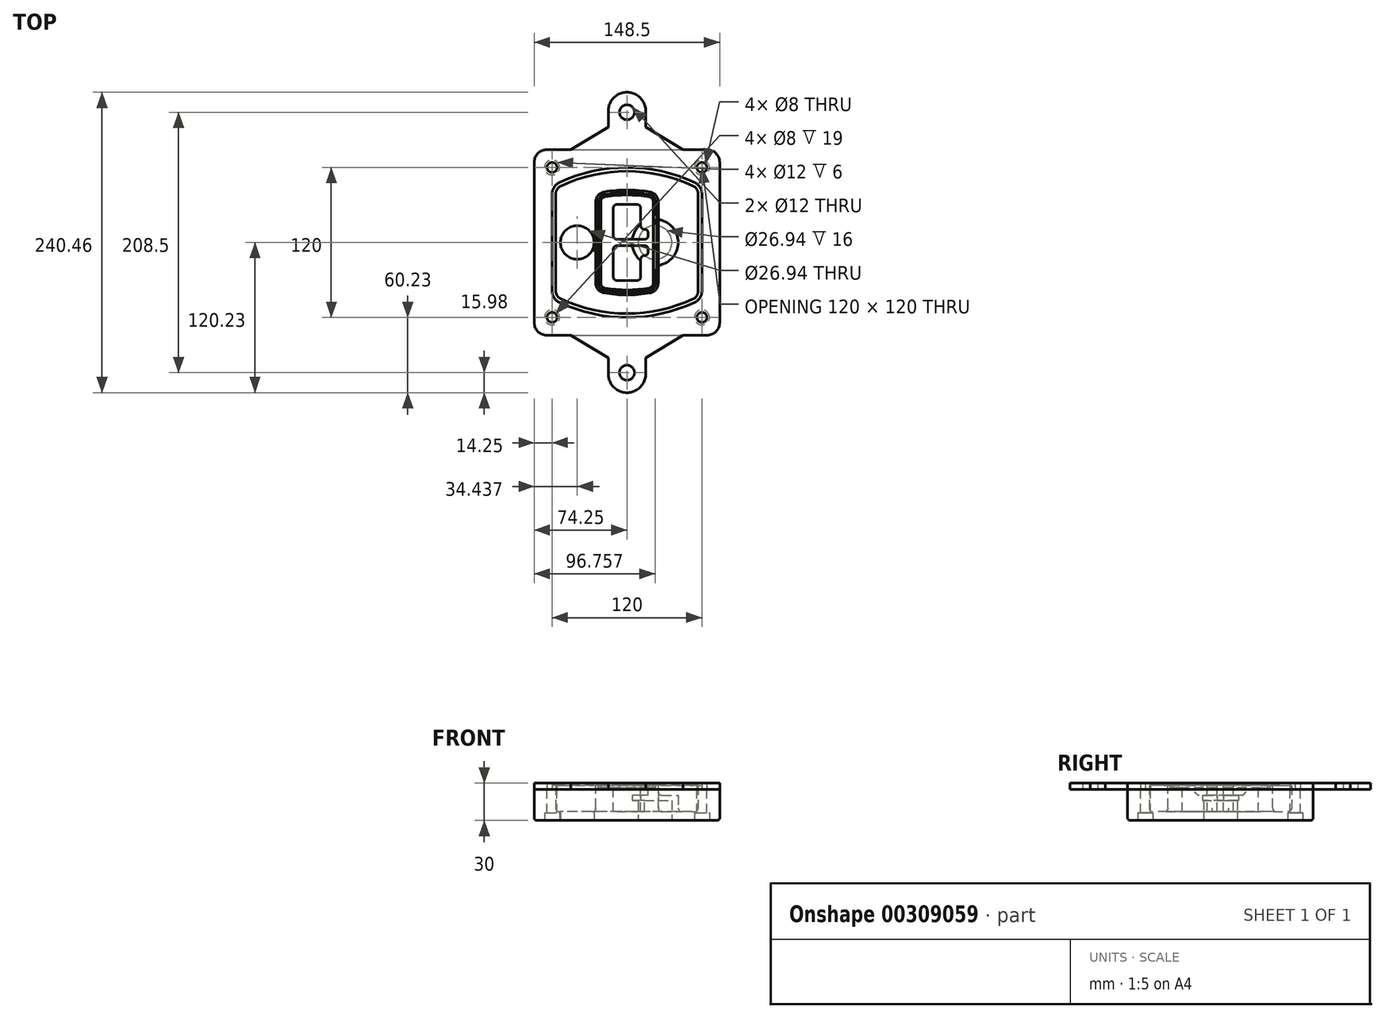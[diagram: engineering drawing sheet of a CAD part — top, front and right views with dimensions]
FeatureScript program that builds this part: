
annotation { "Feature Type Name" : "Feature", "Feature Type Description" : "" }
export const myFeature = defineFeature(function(context is Context, id is Id, definition is map)
    precondition{}
    {
        {
            var Q0;
            Q0=qCreatedBy(makeId("Top.planeOp"),FACE);
            var sketch = newSketch(context, id + "F0", { "sketchPlane" : qUnion([Q0])});
            skPoint(sketch, "E0.rect.middle", {"position": v(0, 0) * mm});
            skLineSegment(sketch, "E1.bottom", {"start": v(-64.25, -74.25) * mm, "end": v(64.25, -74.25) * mm});
            skLineSegment(sketch, "E1.top", {"start": v(-64.25, 74.25) * mm, "end": v(64.25, 74.25) * mm});
            skLineSegment(sketch, "E1.left", {"start": v(-74.25, -64.25) * mm, "end": v(-74.25, 64.25) * mm});
            skLineSegment(sketch, "E1.right", {"start": v(74.25, -64.25) * mm, "end": v(74.25, 64.25) * mm});
            skLineSegment(sketch, "E2", {"start": v(-74.25, 74.25) * mm, "end": v(74.25, -74.25) * mm, "construction": true});
            skLineSegment(sketch, "E3", {"start": v(74.25, 74.25) * mm, "end": v(-74.25, -74.25) * mm, "construction": true});
            skCircle(sketch, "E4", {"center": v(-60, 60) * mm, "radius": 4 * mm});
            skCircle(sketch, "E5", {"center": v(60, 60) * mm, "radius": 4 * mm});
            skCircle(sketch, "E6", {"center": v(60, -60) * mm, "radius": 4 * mm});
            skCircle(sketch, "E7", {"center": v(-60, -60) * mm, "radius": 4 * mm});
            skLineSegment(sketch, "E8", {"start": v(-60, 60) * mm, "end": v(60, 60) * mm, "construction": true});
            skLineSegment(sketch, "E9", {"start": v(60, 60) * mm, "end": v(60, -60) * mm, "construction": true});
            skLineSegment(sketch, "E10", {"start": v(60, -60) * mm, "end": v(-60, -60) * mm, "construction": true});
            skLineSegment(sketch, "E11", {"start": v(-60, -60) * mm, "end": v(-60, 60) * mm, "construction": true});
            skLineSegment(sketch, "E12", {"start": v(-60, 38.83) * mm, "end": v(-60, -38.83) * mm});
            skLineSegment(sketch, "E13", {"start": v(60, 38.83) * mm, "end": v(60, -38.83) * mm});
            skArc(sketch, "E14", {"start": v(54.26, 47.88) * mm, "mid": v(0, 60) * mm, "end": v(-54.26, 47.88) * mm});
            skArc(sketch, "E15", {"start": v(-54.26, -47.88) * mm, "mid": v(0, -60) * mm, "end": v(54.26, -47.88) * mm});
            skLineSegment(sketch, "E16", {"start": v(-60, 0) * mm, "end": v(60, 0) * mm, "construction": true});
            skPoint(sketch, "E17.visualSharp", {"position": v(-60, -45) * mm});
            skArc(sketch, "E17.filletArc", {"start": v(-60, -38.83) * mm, "mid": v(-58.44, -44.2) * mm, "end": v(-54.26, -47.88) * mm});
            skPoint(sketch, "E18.visualSharp", {"position": v(-60, 45) * mm});
            skArc(sketch, "E18.filletArc", {"start": v(-54.26, 47.88) * mm, "mid": v(-58.44, 44.2) * mm, "end": v(-60, 38.83) * mm});
            skPoint(sketch, "E19.visualSharp", {"position": v(60, 45) * mm});
            skArc(sketch, "E19.filletArc", {"start": v(60, 38.83) * mm, "mid": v(58.44, 44.2) * mm, "end": v(54.26, 47.88) * mm});
            skPoint(sketch, "E20.visualSharp", {"position": v(60, -45) * mm});
            skArc(sketch, "E20.filletArc", {"start": v(54.26, -47.88) * mm, "mid": v(58.44, -44.2) * mm, "end": v(60, -38.83) * mm});
            skPoint(sketch, "E21.visualSharp", {"position": v(-74.25, 74.25) * mm});
            skArc(sketch, "E21.filletArc", {"start": v(-64.25, 74.25) * mm, "mid": v(-71.32, 71.32) * mm, "end": v(-74.25, 64.25) * mm});
            skPoint(sketch, "E22.visualSharp", {"position": v(74.25, 74.25) * mm});
            skArc(sketch, "E22.filletArc", {"start": v(74.25, 64.25) * mm, "mid": v(71.32, 71.32) * mm, "end": v(64.25, 74.25) * mm});
            skPoint(sketch, "E23.visualSharp", {"position": v(74.25, -74.25) * mm});
            skArc(sketch, "E23.filletArc", {"start": v(64.25, -74.25) * mm, "mid": v(71.32, -71.32) * mm, "end": v(74.25, -64.25) * mm});
            skPoint(sketch, "E24.visualSharp", {"position": v(-74.25, -74.25) * mm});
            skArc(sketch, "E24.filletArc", {"start": v(-74.25, -64.25) * mm, "mid": v(-71.32, -71.32) * mm, "end": v(-64.25, -74.25) * mm});
            skArc(sketch, "E25.0", {"start": v(57, 38.83) * mm, "mid": v(55.9, 42.58) * mm, "end": v(52.98, 45.17) * mm});
            skLineSegment(sketch, "E25.1", {"start": v(57, 38.83) * mm, "end": v(57, -38.83) * mm});
            skArc(sketch, "E25.2", {"start": v(52.98, -45.17) * mm, "mid": v(55.9, -42.58) * mm, "end": v(57, -38.83) * mm});
            skArc(sketch, "E25.3", {"start": v(-52.98, -45.17) * mm, "mid": v(0, -57) * mm, "end": v(52.98, -45.17) * mm});
            skArc(sketch, "E25.4", {"start": v(-57, -38.83) * mm, "mid": v(-55.9, -42.58) * mm, "end": v(-52.98, -45.17) * mm});
            skArc(sketch, "E25.5", {"start": v(52.98, 45.17) * mm, "mid": v(0, 57) * mm, "end": v(-52.98, 45.17) * mm});
            skLineSegment(sketch, "E25.6", {"start": v(-57, 38.83) * mm, "end": v(-57, -38.83) * mm});
            skArc(sketch, "E25.7", {"start": v(-52.98, 45.17) * mm, "mid": v(-55.9, 42.58) * mm, "end": v(-57, 38.83) * mm});
            skArc(sketch, "E26.0", {"start": v(-55.96, 51.5) * mm, "mid": v(-61.82, 46.33) * mm, "end": v(-64, 38.83) * mm});
            skArc(sketch, "E26.1", {"start": v(55.96, 51.5) * mm, "mid": v(0, 64) * mm, "end": v(-55.96, 51.5) * mm});
            skArc(sketch, "E26.2", {"start": v(64, 38.83) * mm, "mid": v(61.82, 46.33) * mm, "end": v(55.96, 51.5) * mm});
            skLineSegment(sketch, "E26.3", {"start": v(64, 38.83) * mm, "end": v(64, -38.83) * mm});
            skArc(sketch, "E26.4", {"start": v(55.96, -51.5) * mm, "mid": v(61.82, -46.33) * mm, "end": v(64, -38.83) * mm});
            skLineSegment(sketch, "E26.5", {"start": v(-64, 38.83) * mm, "end": v(-64, -38.83) * mm});
            skArc(sketch, "E26.6", {"start": v(-55.96, -51.5) * mm, "mid": v(0, -64) * mm, "end": v(55.96, -51.5) * mm});
            skArc(sketch, "E26.7", {"start": v(-64, -38.83) * mm, "mid": v(-61.82, -46.33) * mm, "end": v(-55.96, -51.5) * mm});
            skSolve(sketch);
        }
        {
            var Q0;
            Q0=makeQuery(id+"F0.imprint","IMPRINT",FACE,{"disambiguationData":[TD([[makeQuery(id+"F0.imprint","IMPRINT",EDGE,{"derivedFrom":sQuery(id+"F0.wireOp",EDGE,"E1.bottom")}),1.0]])]});
            var Q1;
            Q1=makeQuery(id+"F0.imprint","IMPRINT",FACE,{"disambiguationData":[TD([[makeQuery(id+"F0.imprint","IMPRINT",EDGE,{"derivedFrom":sQuery(id+"F0.wireOp",EDGE,"E12")}),1.0]])]});
            var Q2;
            Q2=makeQuery(id+"F0.imprint","IMPRINT",FACE,{"disambiguationData":[TD([[makeQuery(id+"F0.imprint","IMPRINT",EDGE,{"derivedFrom":sQuery(id+"F0.wireOp",EDGE,"E25.0")}),1.0]])]});
            var Q3;
            Q3=makeQuery(id+"F0.imprint","IMPRINT",FACE,{"disambiguationData":[TD([[makeQuery(id+"F0.imprint","IMPRINT",EDGE,{"derivedFrom":sQuery(id+"F0.wireOp",EDGE,"E12")}),-1.0]])]});
            extrude(context, id + "F1", {"entities" : qUnion([Q0, Q1, Q2, Q3]), "oppositeDirection" : true, "depth" : 25 * mm});
        }
        {
            var Q0;
            Q0=makeQuery(id+"F0.imprint","IMPRINT",FACE,{"disambiguationData":[TD([[makeQuery(id+"F0.imprint","IMPRINT",EDGE,{"derivedFrom":sQuery(id+"F0.wireOp",EDGE,"E12")}),1.0]])]});
            extrude(context, id + "F2", {"entities" : qUnion([Q0]), "operationType" : NewBodyOperationType.ADD, "depth" : 3 * mm});
        }
        {
            var Q0;
            Q0=makeQuery(id+"F0.imprint","IMPRINT",FACE,{"disambiguationData":[TD([[makeQuery(id+"F0.imprint","IMPRINT",EDGE,{"derivedFrom":sQuery(id+"F0.wireOp",EDGE,"E25.0")}),1.0]])]});
            extrude(context, id + "F3", {"entities" : qUnion([Q0]), "operationType" : NewBodyOperationType.REMOVE, "oppositeDirection" : true, "depth" : 18 * mm});
        }
        {
            var Q0;
            Q0=makeQuery(id+"F2.opExtrude","CAP_FACE",FACE,{"disambiguationData":[OSD([sQuery(id+"F0.wireOp",EDGE,"E12"),sQuery(id+"F0.wireOp",EDGE,"E13"),sQuery(id+"F0.wireOp",EDGE,"E14"),sQuery(id+"F0.wireOp",EDGE,"E15"),sQuery(id+"F0.wireOp",EDGE,"E17.filletArc"),sQuery(id+"F0.wireOp",EDGE,"E18.filletArc"),sQuery(id+"F0.wireOp",EDGE,"E19.filletArc"),sQuery(id+"F0.wireOp",EDGE,"E20.filletArc"),sQuery(id+"F0.wireOp",EDGE,"E25.0"),sQuery(id+"F0.wireOp",EDGE,"E25.1"),sQuery(id+"F0.wireOp",EDGE,"E25.2"),sQuery(id+"F0.wireOp",EDGE,"E25.3"),sQuery(id+"F0.wireOp",EDGE,"E25.4"),sQuery(id+"F0.wireOp",EDGE,"E25.5"),sQuery(id+"F0.wireOp",EDGE,"E25.6"),sQuery(id+"F0.wireOp",EDGE,"E25.7")])],"isStart":false});
            var sketch = newSketch(context, id + "F4", { "sketchPlane" : qUnion([Q0])});
            skArc(sketch, "E27.0", {"start": v(-18.34, -40.45) * mm, "mid": v(0, -42) * mm, "end": v(18.34, -40.45) * mm});
            skArc(sketch, "E28.0", {"start": v(18.34, 40.45) * mm, "mid": v(0, 42) * mm, "end": v(-18.34, 40.45) * mm});
            skLineSegment(sketch, "E29", {"start": v(-25, 32.57) * mm, "end": v(-25, -32.57) * mm});
            skLineSegment(sketch, "E30", {"start": v(25, 32.57) * mm, "end": v(25, -32.57) * mm});
            skLineSegment(sketch, "E31", {"start": v(-25, 39.1) * mm, "end": v(25, 39.1) * mm, "construction": true});
            skLineSegment(sketch, "E32", {"start": v(-25, -39.1) * mm, "end": v(25, -39.1) * mm, "construction": true});
            skPoint(sketch, "E33.visualSharp", {"position": v(-25, 39.1) * mm});
            skArc(sketch, "E33.filletArc", {"start": v(-18.34, 40.45) * mm, "mid": v(-23.11, 37.73) * mm, "end": v(-25, 32.57) * mm});
            skPoint(sketch, "E34.visualSharp", {"position": v(25, 39.1) * mm});
            skArc(sketch, "E34.filletArc", {"start": v(25, 32.57) * mm, "mid": v(23.11, 37.73) * mm, "end": v(18.34, 40.45) * mm});
            skPoint(sketch, "E35.visualSharp", {"position": v(25, -39.1) * mm});
            skArc(sketch, "E35.filletArc", {"start": v(18.34, -40.45) * mm, "mid": v(23.11, -37.73) * mm, "end": v(25, -32.57) * mm});
            skPoint(sketch, "E36.visualSharp", {"position": v(-25, -39.1) * mm});
            skArc(sketch, "E36.filletArc", {"start": v(-25, -32.57) * mm, "mid": v(-23.11, -37.73) * mm, "end": v(-18.34, -40.45) * mm});
            skArc(sketch, "E37.0", {"start": v(52.98, 45.17) * mm, "mid": v(0, 57) * mm, "end": v(-52.98, 45.17) * mm});
            skArc(sketch, "E37.1", {"start": v(-52.98, 45.17) * mm, "mid": v(-55.9, 42.58) * mm, "end": v(-57, 38.83) * mm});
            skLineSegment(sketch, "E37.2", {"start": v(-57, 38.83) * mm, "end": v(-57, -38.83) * mm});
            skArc(sketch, "E37.3", {"start": v(-57, -38.83) * mm, "mid": v(-55.9, -42.58) * mm, "end": v(-52.98, -45.17) * mm});
            skArc(sketch, "E37.4", {"start": v(-52.98, -45.17) * mm, "mid": v(0, -57) * mm, "end": v(52.98, -45.17) * mm});
            skArc(sketch, "E37.5", {"start": v(52.98, -45.17) * mm, "mid": v(55.9, -42.58) * mm, "end": v(57, -38.83) * mm});
            skLineSegment(sketch, "E37.6", {"start": v(57, 38.83) * mm, "end": v(57, -38.83) * mm});
            skArc(sketch, "E37.7", {"start": v(57, 38.83) * mm, "mid": v(55.9, 42.58) * mm, "end": v(52.98, 45.17) * mm});
            skLineSegment(sketch, "E38.0", {"start": v(23, 32.57) * mm, "end": v(23, -32.57) * mm});
            skArc(sketch, "E38.1", {"start": v(18, -38.48) * mm, "mid": v(21.58, -36.44) * mm, "end": v(23, -32.57) * mm});
            skArc(sketch, "E38.2", {"start": v(-18, -38.48) * mm, "mid": v(0, -40) * mm, "end": v(18, -38.48) * mm});
            skArc(sketch, "E38.3", {"start": v(-23, -32.57) * mm, "mid": v(-21.58, -36.44) * mm, "end": v(-18, -38.48) * mm});
            skLineSegment(sketch, "E38.4", {"start": v(-23, 32.57) * mm, "end": v(-23, -32.57) * mm});
            skArc(sketch, "E38.5", {"start": v(23, 32.57) * mm, "mid": v(21.58, 36.44) * mm, "end": v(18, 38.48) * mm});
            skArc(sketch, "E38.6", {"start": v(-18, 38.48) * mm, "mid": v(-21.58, 36.44) * mm, "end": v(-23, 32.57) * mm});
            skArc(sketch, "E38.7", {"start": v(18, 38.48) * mm, "mid": v(0, 40) * mm, "end": v(-18, 38.48) * mm});
            skArc(sketch, "E39.0", {"start": v(21, 32.57) * mm, "mid": v(20.06, 35.15) * mm, "end": v(17.67, 36.5) * mm});
            skLineSegment(sketch, "E39.1", {"start": v(21, 32.57) * mm, "end": v(21, -32.57) * mm});
            skArc(sketch, "E39.2", {"start": v(17.67, -36.5) * mm, "mid": v(20.06, -35.15) * mm, "end": v(21, -32.57) * mm});
            skArc(sketch, "E39.3", {"start": v(-17.67, -36.5) * mm, "mid": v(0, -38) * mm, "end": v(17.67, -36.5) * mm});
            skArc(sketch, "E39.4", {"start": v(-21, -32.57) * mm, "mid": v(-20.06, -35.15) * mm, "end": v(-17.67, -36.5) * mm});
            skArc(sketch, "E39.5", {"start": v(17.67, 36.5) * mm, "mid": v(0, 38) * mm, "end": v(-17.67, 36.5) * mm});
            skLineSegment(sketch, "E39.6", {"start": v(-21, 32.57) * mm, "end": v(-21, -32.57) * mm});
            skArc(sketch, "E39.7", {"start": v(-17.67, 36.5) * mm, "mid": v(-20.06, 35.15) * mm, "end": v(-21, 32.57) * mm});
            skLineSegment(sketch, "E40", {"start": v(-25, 0) * mm, "end": v(25, 0) * mm, "construction": true});
            skLineSegment(sketch, "E41", {"start": v(-11, 5.5) * mm, "end": v(-11, 27.5) * mm});
            skLineSegment(sketch, "E42", {"start": v(-8, 30.5) * mm, "end": v(8, 30.5) * mm});
            skLineSegment(sketch, "E43", {"start": v(11, 27.5) * mm, "end": v(11, 13.5) * mm});
            skLineSegment(sketch, "E44", {"start": v(14, 10.5) * mm, "end": v(14, 10.5) * mm});
            skLineSegment(sketch, "E45", {"start": v(17, 7.5) * mm, "end": v(17, 5.5) * mm});
            skLineSegment(sketch, "E46", {"start": v(14, 2.5) * mm, "end": v(-8, 2.5) * mm});
            skPoint(sketch, "E47.visualSharp", {"position": v(-11, 30.5) * mm});
            skArc(sketch, "E47.filletArc", {"start": v(-8, 30.5) * mm, "mid": v(-10.12, 29.62) * mm, "end": v(-11, 27.5) * mm});
            skPoint(sketch, "E48.visualSharp", {"position": v(11, 30.5) * mm});
            skArc(sketch, "E48.filletArc", {"start": v(11, 27.5) * mm, "mid": v(10.12, 29.62) * mm, "end": v(8, 30.5) * mm});
            skPoint(sketch, "E49.visualSharp", {"position": v(11, 10.5) * mm});
            skArc(sketch, "E49.filletArc", {"start": v(11, 13.5) * mm, "mid": v(11.88, 11.38) * mm, "end": v(14, 10.5) * mm});
            skPoint(sketch, "E50.visualSharp", {"position": v(17, 10.5) * mm});
            skArc(sketch, "E50.filletArc", {"start": v(17, 7.5) * mm, "mid": v(16.12, 9.62) * mm, "end": v(14, 10.5) * mm});
            skPoint(sketch, "E51.visualSharp", {"position": v(17, 2.5) * mm});
            skArc(sketch, "E51.filletArc", {"start": v(14, 2.5) * mm, "mid": v(16.12, 3.38) * mm, "end": v(17, 5.5) * mm});
            skPoint(sketch, "E52.visualSharp", {"position": v(-11, 2.5) * mm});
            skArc(sketch, "E52.filletArc", {"start": v(-11, 5.5) * mm, "mid": v(-10.12, 3.38) * mm, "end": v(-8, 2.5) * mm});
            skLineSegment(sketch, "E53.0.MirrorCS", {"start": v(14, -2.5) * mm, "end": v(-8, -2.5) * mm});
            skArc(sketch, "E54.0.MirrorCS", {"start": v(-11, -5.5) * mm, "mid": v(-10.12, -3.38) * mm, "end": v(-8, -2.5) * mm});
            skLineSegment(sketch, "E55.0.MirrorCS", {"start": v(-11, -5.5) * mm, "end": v(-11, -27.5) * mm});
            skArc(sketch, "E56.0.MirrorCS", {"start": v(-8, -30.5) * mm, "mid": v(-10.12, -29.62) * mm, "end": v(-11, -27.5) * mm});
            skLineSegment(sketch, "E57.0.MirrorCS", {"start": v(-8, -30.5) * mm, "end": v(8, -30.5) * mm});
            skArc(sketch, "E58.0.MirrorCS", {"start": v(11, -27.5) * mm, "mid": v(10.12, -29.62) * mm, "end": v(8, -30.5) * mm});
            skLineSegment(sketch, "E59.0.MirrorCS", {"start": v(11, -27.5) * mm, "end": v(11, -13.5) * mm});
            skArc(sketch, "E60.0.MirrorCS", {"start": v(11, -13.5) * mm, "mid": v(11.88, -11.38) * mm, "end": v(14, -10.5) * mm});
            skArc(sketch, "E61.0.MirrorCS", {"start": v(17, -7.5) * mm, "mid": v(16.12, -9.62) * mm, "end": v(14, -10.5) * mm});
            skLineSegment(sketch, "E62.0.MirrorCS", {"start": v(17, -7.5) * mm, "end": v(17, -5.5) * mm});
            skArc(sketch, "E63.0.MirrorCS", {"start": v(14, -2.5) * mm, "mid": v(16.12, -3.38) * mm, "end": v(17, -5.5) * mm});
            skSolve(sketch);
        }
        {
            var Q0;
            Q0=makeQuery(id+"F4.imprint","IMPRINT",FACE,{"disambiguationData":[TD([[makeQuery(id+"F4.imprint","IMPRINT",EDGE,{"derivedFrom":sQuery(id+"F4.wireOp",EDGE,"E27.0")}),1.0]])]});
            var Q1;
            Q1=makeQuery(id+"F4.imprint","IMPRINT",FACE,{"disambiguationData":[TD([[makeQuery(id+"F4.imprint","IMPRINT",EDGE,{"derivedFrom":sQuery(id+"F4.wireOp",EDGE,"E38.0")}),-1.0]])]});
            var Q2;
            Q2=makeQuery(id+"F4.imprint","IMPRINT",FACE,{"disambiguationData":[TD([[makeQuery(id+"F4.imprint","IMPRINT",EDGE,{"derivedFrom":sQuery(id+"F4.wireOp",EDGE,"E39.0")}),1.0]])]});
            extrude(context, id + "F5", {"entities" : qUnion([Q0, Q1, Q2]), "operationType" : NewBodyOperationType.ADD, "endBound" : BoundingType.UP_TO_NEXT, "oppositeDirection" : true, "depth" : 25 * mm});
        }
        {
            var Q0;
            Q0=makeQuery(id+"F4.imprint","IMPRINT",FACE,{"disambiguationData":[TD([[makeQuery(id+"F4.imprint","IMPRINT",EDGE,{"derivedFrom":sQuery(id+"F4.wireOp",EDGE,"E38.0")}),-1.0]])]});
            extrude(context, id + "F6", {"entities" : qUnion([Q0]), "operationType" : NewBodyOperationType.REMOVE, "oppositeDirection" : true, "depth" : 2 * mm});
        }
        {
            var Q0;
            Q0=makeQuery(id+"F1.opExtrude","CAP_FACE",FACE,{"disambiguationData":[OSD([sQuery(id+"F0.wireOp",EDGE,"E1.bottom"),sQuery(id+"F0.wireOp",EDGE,"E1.top"),sQuery(id+"F0.wireOp",EDGE,"E1.left"),sQuery(id+"F0.wireOp",EDGE,"E1.right"),sQuery(id+"F0.wireOp",EDGE,"E4"),sQuery(id+"F0.wireOp",EDGE,"E5"),sQuery(id+"F0.wireOp",EDGE,"E6"),sQuery(id+"F0.wireOp",EDGE,"E7"),sQuery(id+"F0.wireOp",EDGE,"E21.filletArc"),sQuery(id+"F0.wireOp",EDGE,"E22.filletArc"),sQuery(id+"F0.wireOp",EDGE,"E23.filletArc"),sQuery(id+"F0.wireOp",EDGE,"E24.filletArc")])],"isStart":false});
            var sketch = newSketch(context, id + "F7", { "sketchPlane" : qUnion([Q0])});
            skCircle(sketch, "E64", {"center": v(22.5, 0) * mm, "radius": 13.47 * mm});
            skCircle(sketch, "E65", {"center": v(-39.81, 0) * mm, "radius": 13.47 * mm});
            skLineSegment(sketch, "E66", {"start": v(74.25, 0) * mm, "end": v(-74.25, 0) * mm});
            skCircle(sketch, "E67", {"center": v(22.5, 0) * mm, "radius": 18.47 * mm});
            skCircle(sketch, "E68", {"center": v(60, -60) * mm, "radius": 6 * mm});
            skCircle(sketch, "E69", {"center": v(-60, -60) * mm, "radius": 6 * mm});
            skCircle(sketch, "E70", {"center": v(-60, 60) * mm, "radius": 6 * mm});
            skCircle(sketch, "E71", {"center": v(60, 60) * mm, "radius": 6 * mm});
            skSolve(sketch);
        }
        {
            var Q0;
            {var subQ1=sQuery(id+"F7.wireOp",EDGE,"E66");var subQ4=sQuery(id+"F7.wireOp",EDGE,"E64");var subQ6=makeQuery(id+"F7.imprint","INTERSECT",VERTEX,{"disambiguationData":[OD(0.0)],"derivedFrom":[subQ4,subQ1]});Q0=makeQuery(id+"F7.imprint","IMPRINT",FACE,{"disambiguationData":[TD([[makeQuery(id+"F7.imprint","IMPRINT",EDGE,{"disambiguationData":[TD([[subQ6,-1.0]])],"derivedFrom":subQ4}),-1.0]])]});}
            var Q1;
            {var subQ0=sQuery(id+"F7.wireOp",EDGE,"E66");var subQ1=sQuery(id+"F7.wireOp",EDGE,"E64");var subQ3=makeQuery(id+"F7.imprint","INTERSECT",VERTEX,{"disambiguationData":[OD(0.0)],"derivedFrom":[subQ1,subQ0]});Q1=makeQuery(id+"F7.imprint","IMPRINT",FACE,{"disambiguationData":[TD([[makeQuery(id+"F7.imprint","IMPRINT",EDGE,{"disambiguationData":[TD([[subQ3,-1.0]])],"derivedFrom":subQ1}),1.0]])]});}
            var Q2;
            {var subQ0=sQuery(id+"F7.wireOp",EDGE,"E66");var subQ1=sQuery(id+"F7.wireOp",EDGE,"E64");var subQ3=makeQuery(id+"F7.imprint","INTERSECT",VERTEX,{"disambiguationData":[OD(0.0)],"derivedFrom":[subQ1,subQ0]});Q2=makeQuery(id+"F7.imprint","IMPRINT",FACE,{"disambiguationData":[TD([[makeQuery(id+"F7.imprint","IMPRINT",EDGE,{"disambiguationData":[TD([[subQ3,1.0]])],"derivedFrom":subQ1}),1.0]])]});}
            var Q3;
            {var subQ1=sQuery(id+"F7.wireOp",EDGE,"E66");var subQ4=sQuery(id+"F7.wireOp",EDGE,"E64");var subQ6=makeQuery(id+"F7.imprint","INTERSECT",VERTEX,{"disambiguationData":[OD(0.0)],"derivedFrom":[subQ4,subQ1]});Q3=makeQuery(id+"F7.imprint","IMPRINT",FACE,{"disambiguationData":[TD([[makeQuery(id+"F7.imprint","IMPRINT",EDGE,{"disambiguationData":[TD([[subQ6,1.0]])],"derivedFrom":subQ4}),-1.0]])]});}
            extrude(context, id + "F8", {"entities" : qUnion([Q0, Q1, Q2, Q3]), "operationType" : NewBodyOperationType.ADD, "oppositeDirection" : true, "depth" : 20 * mm});
        }
        {
            var Q0;
            {var subQ0=sQuery(id+"F7.wireOp",EDGE,"E66");var subQ1=sQuery(id+"F7.wireOp",EDGE,"E64");var subQ3=makeQuery(id+"F7.imprint","INTERSECT",VERTEX,{"disambiguationData":[OD(0.0)],"derivedFrom":[subQ1,subQ0]});Q0=makeQuery(id+"F7.imprint","IMPRINT",FACE,{"disambiguationData":[TD([[makeQuery(id+"F7.imprint","IMPRINT",EDGE,{"disambiguationData":[TD([[subQ3,-1.0]])],"derivedFrom":subQ1}),1.0]])]});}
            var Q1;
            {var subQ0=sQuery(id+"F7.wireOp",EDGE,"E66");var subQ1=sQuery(id+"F7.wireOp",EDGE,"E64");var subQ3=makeQuery(id+"F7.imprint","INTERSECT",VERTEX,{"disambiguationData":[OD(0.0)],"derivedFrom":[subQ1,subQ0]});Q1=makeQuery(id+"F7.imprint","IMPRINT",FACE,{"disambiguationData":[TD([[makeQuery(id+"F7.imprint","IMPRINT",EDGE,{"disambiguationData":[TD([[subQ3,1.0]])],"derivedFrom":subQ1}),1.0]])]});}
            extrude(context, id + "F9", {"entities" : qUnion([Q0, Q1]), "operationType" : NewBodyOperationType.REMOVE, "oppositeDirection" : true, "depth" : 16 * mm});
        }
        {
            var Q0;
            {var subQ0=sQuery(id+"F7.wireOp",EDGE,"E66");var subQ1=sQuery(id+"F7.wireOp",EDGE,"E65");var subQ3=makeQuery(id+"F7.imprint","INTERSECT",VERTEX,{"disambiguationData":[OD(0.0)],"derivedFrom":[subQ1,subQ0]});Q0=makeQuery(id+"F7.imprint","IMPRINT",FACE,{"disambiguationData":[TD([[makeQuery(id+"F7.imprint","IMPRINT",EDGE,{"disambiguationData":[TD([[subQ3,-1.0]])],"derivedFrom":subQ1}),1.0]])]});}
            var Q1;
            {var subQ0=sQuery(id+"F7.wireOp",EDGE,"E66");var subQ1=sQuery(id+"F7.wireOp",EDGE,"E65");var subQ3=makeQuery(id+"F7.imprint","INTERSECT",VERTEX,{"disambiguationData":[OD(0.0)],"derivedFrom":[subQ1,subQ0]});Q1=makeQuery(id+"F7.imprint","IMPRINT",FACE,{"disambiguationData":[TD([[makeQuery(id+"F7.imprint","IMPRINT",EDGE,{"disambiguationData":[TD([[subQ3,1.0]])],"derivedFrom":subQ1}),1.0]])]});}
            extrude(context, id + "F10", {"entities" : qUnion([Q0, Q1]), "operationType" : NewBodyOperationType.REMOVE, "oppositeDirection" : true, "depth" : 25 * mm});
        }
        {
            var Q0;
            Q0=makeQuery(id+"F7.imprint","IMPRINT",FACE,{"disambiguationData":[TD([[makeQuery(id+"F7.imprint","IMPRINT",EDGE,{"derivedFrom":sQuery(id+"F7.wireOp",EDGE,"E68")}),1.0]])]});
            var Q1;
            Q1=makeQuery(id+"F7.imprint","IMPRINT",FACE,{"disambiguationData":[TD([[makeQuery(id+"F7.imprint","IMPRINT",EDGE,{"derivedFrom":makeQuery(id+"F1.opExtrude","CAP_EDGE",EDGE,{"disambiguationData":[OSD([sQuery(id+"F0.wireOp",EDGE,"E5")])],"isStart":false})}),-1.0]])]});
            var Q2;
            Q2=makeQuery(id+"F7.imprint","IMPRINT",FACE,{"disambiguationData":[TD([[makeQuery(id+"F7.imprint","IMPRINT",EDGE,{"derivedFrom":sQuery(id+"F7.wireOp",EDGE,"E69")}),1.0]])]});
            var Q3;
            Q3=makeQuery(id+"F7.imprint","IMPRINT",FACE,{"disambiguationData":[TD([[makeQuery(id+"F7.imprint","IMPRINT",EDGE,{"derivedFrom":makeQuery(id+"F1.opExtrude","CAP_EDGE",EDGE,{"disambiguationData":[OSD([sQuery(id+"F0.wireOp",EDGE,"E4")])],"isStart":false})}),-1.0]])]});
            var Q4;
            Q4=makeQuery(id+"F7.imprint","IMPRINT",FACE,{"disambiguationData":[TD([[makeQuery(id+"F7.imprint","IMPRINT",EDGE,{"derivedFrom":sQuery(id+"F7.wireOp",EDGE,"E70")}),1.0]])]});
            var Q5;
            Q5=makeQuery(id+"F7.imprint","IMPRINT",FACE,{"disambiguationData":[TD([[makeQuery(id+"F7.imprint","IMPRINT",EDGE,{"derivedFrom":makeQuery(id+"F1.opExtrude","CAP_EDGE",EDGE,{"disambiguationData":[OSD([sQuery(id+"F0.wireOp",EDGE,"E7")])],"isStart":false})}),-1.0]])]});
            var Q6;
            Q6=makeQuery(id+"F7.imprint","IMPRINT",FACE,{"disambiguationData":[TD([[makeQuery(id+"F7.imprint","IMPRINT",EDGE,{"derivedFrom":sQuery(id+"F7.wireOp",EDGE,"E71")}),1.0]])]});
            var Q7;
            Q7=makeQuery(id+"F7.imprint","IMPRINT",FACE,{"disambiguationData":[TD([[makeQuery(id+"F7.imprint","IMPRINT",EDGE,{"derivedFrom":makeQuery(id+"F1.opExtrude","CAP_EDGE",EDGE,{"disambiguationData":[OSD([sQuery(id+"F0.wireOp",EDGE,"E6")])],"isStart":false})}),-1.0]])]});
            extrude(context, id + "F11", {"entities" : qUnion([Q0, Q1, Q2, Q3, Q4, Q5, Q6, Q7]), "operationType" : NewBodyOperationType.REMOVE, "oppositeDirection" : true, "depth" : 6 * mm});
        }
        {
            var Q0;
            Q0=makeQuery(id+"F9.boolean.opBoolean","COPY",FACE,{"derivedFrom":makeQuery(id+"F9.opExtrude","CAP_FACE",FACE,{"disambiguationData":[OSD([sQuery(id+"F7.wireOp",EDGE,"E64")])],"isStart":false})});
            var sketch = newSketch(context, id + "F12", { "sketchPlane" : qUnion([Q0])});
            skArc(sketch, "E72.0", {"start": v(11, 14.45) * mm, "mid": v(6.45, 9.13) * mm, "end": v(4.2, 2.5) * mm});
            skArc(sketch, "E72.1", {"start": v(4.2, -2.5) * mm, "mid": v(6.45, -9.13) * mm, "end": v(11, -14.45) * mm});
            skLineSegment(sketch, "E73", {"start": v(4.2, -2.5) * mm, "end": v(14, -2.5) * mm});
            skLineSegment(sketch, "E74.0", {"start": v(14, 2.5) * mm, "end": v(4.2, 2.5) * mm});
            skArc(sketch, "E74.1", {"start": v(14, 2.5) * mm, "mid": v(16.12, 3.38) * mm, "end": v(17, 5.5) * mm});
            skLineSegment(sketch, "E74.2", {"start": v(17, 7.5) * mm, "end": v(17, 5.5) * mm});
            skArc(sketch, "E74.3", {"start": v(17, 7.5) * mm, "mid": v(16.12, 9.62) * mm, "end": v(14, 10.5) * mm});
            skArc(sketch, "E74.4", {"start": v(11, 13.5) * mm, "mid": v(11.88, 11.38) * mm, "end": v(14, 10.5) * mm});
            skLineSegment(sketch, "E74.5", {"start": v(11, 14.45) * mm, "end": v(11, 13.5) * mm});
            skLineSegment(sketch, "E74.7", {"start": v(14, -2.5) * mm, "end": v(4.2, -2.5) * mm});
            skArc(sketch, "E74.8", {"start": v(14, -2.5) * mm, "mid": v(16.12, -3.38) * mm, "end": v(17, -5.5) * mm});
            skLineSegment(sketch, "E74.9", {"start": v(17, -7.5) * mm, "end": v(17, -5.5) * mm});
            skArc(sketch, "E74.10", {"start": v(17, -7.5) * mm, "mid": v(16.12, -9.62) * mm, "end": v(14, -10.5) * mm});
            skArc(sketch, "E74.11", {"start": v(11, -13.5) * mm, "mid": v(11.88, -11.38) * mm, "end": v(14, -10.5) * mm});
            skLineSegment(sketch, "E74.12", {"start": v(11, -14.45) * mm, "end": v(11, -13.5) * mm});
            skPoint(sketch, "E75.orphan", {"position": v(11, -27.5) * mm});
            skPoint(sketch, "E76.orphan", {"position": v(-8, -2.5) * mm});
            skPoint(sketch, "E77.orphan", {"position": v(-8, 2.5) * mm});
            skPoint(sketch, "E78.orphan", {"position": v(11, 27.5) * mm});
            skSolve(sketch);
        }
        {
            var Q0;
            {var subQ7=sQuery(id+"F12.wireOp",EDGE,"E72.0");var subQ14=sQuery(id+"F12.wireOp",EDGE,"E72.1");var subQ16=sQuery(id+"F12.wireOp",EDGE,"E74.1");var subQ18=sQuery(id+"F12.wireOp",EDGE,"E74.8");Q0=qUnion([makeQuery(id+"F12.imprint","IMPRINT",FACE,{"disambiguationData":[TD([[makeQuery(id+"F12.imprint","IMPRINT",EDGE,{"derivedFrom":subQ7}),1.0]])]}),makeQuery(id+"F12.imprint","IMPRINT",FACE,{"disambiguationData":[TD([[makeQuery(id+"F12.imprint","IMPRINT",EDGE,{"derivedFrom":subQ14}),1.0]])]}),makeQuery(id+"F12.imprint","IMPRINT",FACE,{"disambiguationData":[TD([[makeQuery(id+"F12.imprint","IMPRINT",EDGE,{"derivedFrom":subQ16}),1.0]])]}),makeQuery(id+"F12.imprint","IMPRINT",FACE,{"disambiguationData":[TD([[makeQuery(id+"F12.imprint","IMPRINT",EDGE,{"derivedFrom":subQ18}),-1.0]])]})]);}
            var Q1;
            Q1=makeQuery(id+"F5.boolean.opBoolean","SPLIT",FACE,{"disambiguationData":[TD([makeQuery(id+"F5.opExtrude","SWEPT_FACE",FACE,{"disambiguationData":[OSD([sQuery(id+"F4.wireOp",EDGE,"E41")])]})])],"derivedFrom":makeQuery(id+"F3.boolean.opBoolean","COPY",FACE,{"derivedFrom":makeQuery(id+"F3.opExtrude","CAP_FACE",FACE,{"disambiguationData":[OSD([sQuery(id+"F0.wireOp",EDGE,"E25.0"),sQuery(id+"F0.wireOp",EDGE,"E25.1"),sQuery(id+"F0.wireOp",EDGE,"E25.2"),sQuery(id+"F0.wireOp",EDGE,"E25.3"),sQuery(id+"F0.wireOp",EDGE,"E25.4"),sQuery(id+"F0.wireOp",EDGE,"E25.5"),sQuery(id+"F0.wireOp",EDGE,"E25.6"),sQuery(id+"F0.wireOp",EDGE,"E25.7")])],"isStart":false})})});
            extrude(context, id + "F13", {"entities" : qUnion([Q0]), "operationType" : NewBodyOperationType.REMOVE, "endBound" : BoundingType.UP_TO_SURFACE, "endBoundEntityFace" : qUnion([Q1]), "depth" : 25 * mm});
        }
        {
            var Q0;
            Q0=makeQuery(id+"F3.boolean.opBoolean","COPY",EDGE,{"derivedFrom":makeQuery(id+"F3.opExtrude","CAP_EDGE",EDGE,{"disambiguationData":[OSD([sQuery(id+"F0.wireOp",EDGE,"E25.6")])],"isStart":false})});
            var Q1;
            Q1=makeQuery(id+"F8.boolean.opBoolean","INTERSECT",EDGE,{"derivedFrom":[makeQuery(id+"F5.opExtrude","SWEPT_FACE",FACE,{"disambiguationData":[OSD([sQuery(id+"F4.wireOp",EDGE,"E30")])]}),makeQuery(id+"F8.opExtrude","CAP_FACE",FACE,{"disambiguationData":[OSD([sQuery(id+"F7.wireOp",EDGE,"E67")])],"isStart":false})]});
            var Q2;
            Q2=makeQuery(id+"F8.boolean.opBoolean","INTERSECT",EDGE,{"disambiguationData":[OD(1.0)],"derivedFrom":[makeQuery(id+"F5.opExtrude","SWEPT_FACE",FACE,{"disambiguationData":[OSD([sQuery(id+"F4.wireOp",EDGE,"E30")])]}),makeQuery(id+"F8.opExtrude","SWEPT_FACE",FACE,{"disambiguationData":[OSD([sQuery(id+"F7.wireOp",EDGE,"E67")])]})]});
            var Q3;
            {var subQ0=sQuery(id+"F4.wireOp",EDGE,"E30");Q3=makeQuery(id+"F8.boolean.opBoolean","SPLIT",EDGE,{"disambiguationData":[TD([makeQuery(id+"F5.opExtrude","SWEPT_FACE",FACE,{"disambiguationData":[OSD([sQuery(id+"F4.wireOp",EDGE,"E35.filletArc")])]})])],"derivedFrom":makeQuery(id+"F5.opExtrude","CAP_EDGE",EDGE,{"disambiguationData":[OSD([subQ0])],"isStart":false})});}
            var Q4;
            {var subQ0=sQuery(id+"F0.wireOp",EDGE,"E25.7");var subQ1=sQuery(id+"F0.wireOp",EDGE,"E25.1");var subQ2=sQuery(id+"F0.wireOp",EDGE,"E25.6");var subQ3=sQuery(id+"F0.wireOp",EDGE,"E25.5");var subQ4=sQuery(id+"F0.wireOp",EDGE,"E25.4");var subQ5=sQuery(id+"F0.wireOp",EDGE,"E25.0");var subQ6=sQuery(id+"F0.wireOp",EDGE,"E25.2");var subQ7=sQuery(id+"F0.wireOp",EDGE,"E25.3");Q4=makeQuery(id+"F8.boolean.opBoolean","INTERSECT",EDGE,{"derivedFrom":[makeQuery(id+"F5.boolean.opBoolean","SPLIT",FACE,{"disambiguationData":[TD([makeQuery(id+"F2.opExtrude","SWEPT_FACE",FACE,{"disambiguationData":[OSD([subQ5])]})])],"derivedFrom":makeQuery(id+"F3.boolean.opBoolean","COPY",FACE,{"derivedFrom":makeQuery(id+"F3.opExtrude","CAP_FACE",FACE,{"disambiguationData":[OSD([subQ5,subQ1,subQ6,subQ7,subQ4,subQ3,subQ2,subQ0])],"isStart":false})})}),makeQuery(id+"F8.opExtrude","SWEPT_FACE",FACE,{"disambiguationData":[OSD([sQuery(id+"F7.wireOp",EDGE,"E67")])]})]});}
            var Q5;
            Q5=makeQuery(id+"F8.boolean.opBoolean","INTERSECT",EDGE,{"disambiguationData":[OD(0.0)],"derivedFrom":[makeQuery(id+"F5.opExtrude","SWEPT_FACE",FACE,{"disambiguationData":[OSD([sQuery(id+"F4.wireOp",EDGE,"E30")])]}),makeQuery(id+"F8.opExtrude","SWEPT_FACE",FACE,{"disambiguationData":[OSD([sQuery(id+"F7.wireOp",EDGE,"E67")])]})]});
            fillet(context, id + "F14", {"entities" : qUnion([Q0, Q1, Q2, Q3, Q4, Q5]), "radius" : 3 * mm, "tangentPropagation" : true, "allowEdgeOverflow" : false});
        }
        {
            var Q0;
            Q0=makeQuery(id+"F1.opExtrude","CAP_EDGE",EDGE,{"disambiguationData":[OSD([sQuery(id+"F0.wireOp",EDGE,"E1.bottom")])],"isStart":false});
            fillet(context, id + "F15", {"entities" : qUnion([Q0]), "radius" : 2 * mm, "tangentPropagation" : true, "allowEdgeOverflow" : false});
        }
        {
            var Q0;
            {var subQ0=sQuery(id+"F0.wireOp",EDGE,"E21.filletArc");var subQ1=sQuery(id+"F0.wireOp",EDGE,"E7");var subQ2=sQuery(id+"F0.wireOp",EDGE,"E6");var subQ3=sQuery(id+"F0.wireOp",EDGE,"E5");var subQ4=sQuery(id+"F0.wireOp",EDGE,"E4");var subQ5=sQuery(id+"F0.wireOp",EDGE,"E22.filletArc");var subQ6=sQuery(id+"F0.wireOp",EDGE,"E1.bottom");var subQ7=sQuery(id+"F0.wireOp",EDGE,"E1.right");var subQ8=sQuery(id+"F0.wireOp",EDGE,"E1.top");var subQ9=sQuery(id+"F0.wireOp",EDGE,"E1.left");var subQ10=sQuery(id+"F0.wireOp",EDGE,"E23.filletArc");var subQ11=sQuery(id+"F0.wireOp",EDGE,"E24.filletArc");Q0=makeQuery(id+"F2.boolean.opBoolean","SPLIT",FACE,{"disambiguationData":[TD([makeQuery(id+"F1.opExtrude","SWEPT_FACE",FACE,{"disambiguationData":[OSD([subQ6])]})])],"derivedFrom":makeQuery(id+"F1.opExtrude","CAP_FACE",FACE,{"disambiguationData":[OSD([subQ6,subQ8,subQ9,subQ7,subQ4,subQ3,subQ2,subQ1,subQ0,subQ5,subQ10,subQ11])],"isStart":true})});}
            var sketch = newSketch(context, id + "F16", { "sketchPlane" : qUnion([Q0])});
            skLineSegment(sketch, "E79", {"start": v(-64.25, 74.25) * mm, "end": v(-64.25, 74.25) * mm});
            skLineSegment(sketch, "E80", {"start": v(-74.25, 64.25) * mm, "end": v(-74.25, 64.25) * mm});
            skLineSegment(sketch, "E81", {"start": v(-74.25, 64.25) * mm, "end": v(-74.25, -64.25) * mm});
            skLineSegment(sketch, "E82", {"start": v(-74.25, -64.25) * mm, "end": v(-74.25, -64.25) * mm});
            skLineSegment(sketch, "E83", {"start": v(-64.25, -74.25) * mm, "end": v(-64.25, -74.25) * mm});
            skLineSegment(sketch, "E84", {"start": v(64.25, -74.25) * mm, "end": v(64.25, -74.25) * mm});
            skLineSegment(sketch, "E85", {"start": v(74.25, -64.25) * mm, "end": v(74.25, -64.25) * mm});
            skLineSegment(sketch, "E86", {"start": v(64.25, 74.25) * mm, "end": v(64.25, 74.25) * mm});
            skLineSegment(sketch, "E87", {"start": v(74.25, 64.25) * mm, "end": v(74.25, 64.25) * mm});
            skLineSegment(sketch, "E88", {"start": v(74.25, 64.25) * mm, "end": v(74.25, -64.25) * mm});
            skPoint(sketch, "E89.visualSharp", {"position": v(-74.25, 74.25) * mm});
            skArc(sketch, "E89.filletArc", {"start": v(-64.25, 74.25) * mm, "mid": v(-71.32, 71.32) * mm, "end": v(-74.25, 64.25) * mm});
            skPoint(sketch, "E90.visualSharp", {"position": v(74.25, 74.25) * mm});
            skArc(sketch, "E90.filletArc", {"start": v(74.25, 64.25) * mm, "mid": v(71.32, 71.32) * mm, "end": v(64.25, 74.25) * mm});
            skPoint(sketch, "E91.visualSharp", {"position": v(74.25, -74.25) * mm});
            skArc(sketch, "E91.filletArc", {"start": v(64.25, -74.25) * mm, "mid": v(71.32, -71.32) * mm, "end": v(74.25, -64.25) * mm});
            skPoint(sketch, "E92.visualSharp", {"position": v(-74.25, -74.25) * mm});
            skArc(sketch, "E92.filletArc", {"start": v(-74.25, -64.25) * mm, "mid": v(-71.32, -71.32) * mm, "end": v(-64.25, -74.25) * mm});
            skCircle(sketch, "E93", {"center": v(0, 104.25) * mm, "radius": 6 * mm});
            skArc(sketch, "E94", {"start": v(14.97, 104.25) * mm, "mid": v(0, 120.23) * mm, "end": v(-14.97, 104.25) * mm});
            skLineSegment(sketch, "E95", {"start": v(-14.97, 92.25) * mm, "end": v(-44.97, 74.25) * mm});
            skLineSegment(sketch, "E96", {"start": v(-14.97, 92.25) * mm, "end": v(-14.97, 104.25) * mm});
            skLineSegment(sketch, "E97", {"start": v(14.97, 92.25) * mm, "end": v(44.97, 74.25) * mm});
            skLineSegment(sketch, "E98", {"start": v(14.97, 104.25) * mm, "end": v(14.97, 92.25) * mm});
            skLineSegment(sketch, "E99.MirrorCS", {"start": v(14.97, -92.25) * mm, "end": v(44.97, -74.25) * mm});
            skLineSegment(sketch, "E100.MirrorCS", {"start": v(14.97, -104.25) * mm, "end": v(14.97, -92.25) * mm});
            skArc(sketch, "E101.MirrorCS", {"start": v(14.97, -104.25) * mm, "mid": v(0, -120.23) * mm, "end": v(-14.97, -104.25) * mm});
            skLineSegment(sketch, "E102.MirrorCS", {"start": v(-14.97, -92.25) * mm, "end": v(-14.97, -104.25) * mm});
            skLineSegment(sketch, "E103.MirrorCS", {"start": v(-14.97, -92.25) * mm, "end": v(-44.97, -74.25) * mm});
            skCircle(sketch, "E104.MirrorC", {"center": v(0, -104.25) * mm, "radius": 6 * mm});
            skLineSegment(sketch, "E105", {"start": v(-64.25, 74.25) * mm, "end": v(-44.97, 74.25) * mm});
            skLineSegment(sketch, "E106", {"start": v(44.97, 74.25) * mm, "end": v(64.25, 74.25) * mm});
            skLineSegment(sketch, "E107", {"start": v(44.97, -74.25) * mm, "end": v(64.25, -74.25) * mm});
            skLineSegment(sketch, "E108", {"start": v(-64.25, -74.25) * mm, "end": v(-44.97, -74.25) * mm});
            skSolve(sketch);
        }
        {
            var Q0;
            Q0=makeQuery(id+"F16.imprint","IMPRINT",FACE,{"disambiguationData":[TD([[makeQuery(id+"F16.imprint","IMPRINT",EDGE,{"derivedFrom":sQuery(id+"F16.wireOp",EDGE,"E93")}),-1.0]])]});
            var Q1;
            {var subQ0=sQuery(id+"F16.wireOp",EDGE,"E99.MirrorCS");Q1=makeQuery(id+"F16.imprint","IMPRINT",FACE,{"disambiguationData":[TD([[makeQuery(id+"F16.imprint","IMPRINT",EDGE,{"derivedFrom":subQ0}),1.0]])]});}
            var Q2;
            Q2=makeQuery(id+"F16.imprint","IMPRINT",FACE,{"disambiguationData":[TD([[makeQuery(id+"F16.imprint","IMPRINT",EDGE,{"derivedFrom":sQuery(id+"F16.wireOp",EDGE,"E81")}),-1.0]])]});
            extrude(context, id + "F17", {"entities" : qUnion([Q0, Q1, Q2]), "depth" : 5 * mm});
        }
    });
